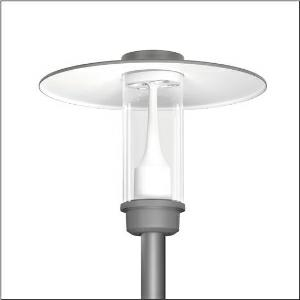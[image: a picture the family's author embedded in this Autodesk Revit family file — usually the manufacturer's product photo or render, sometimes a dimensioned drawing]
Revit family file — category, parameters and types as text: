
# Revit family: litepole_2_iq___p1_0a_5xa5425ff14h_a7e5
name_source: partatom
category: Lighting Fixtures
units: mm (PartAtom-declared; Revit-internal decimal feet)

## family parameters
Cut with Voids When Loaded = No
Host = Face
Light Source = No
Part Type = Normal
Room Calculation Point = No
Round Connector Dimension = Use Diameter
Shared = No

## types (1)
- --- (1 x LED, 1520 lm, 10.5 W, 3000K)
    Apparent Load = 11 VA
    CIE Flux Codes = 33 62 89 96 100
    Color Rendering = 70
    Color Temperature = 3000K
    Default Elevation = 1800 mm
    Description = Litepole 2 iQ, mast luminaire, Module 540 iQ-SR, primary light control with 3 zone facetted reflector, of plastic, silver coated, highly specular, structured, primary optical cover: cover, of PMMA, transparent, light distribution: P1.0a, light emission: direct distribution, primary light characteristic: strongly asymmetric, installation type: post-top, LED, High Power LED, rated luminous flux: 1.520lm, luminous efficacy: 145lm/W, light colour: 730, colour temperature: 3000K, control gear: iQ Street-Remote, control: Auto-Match, Temp-Guard, Lumen-Switch, Night-Set, Smart-Wire, Light-Fading, Desk-Remote (wireless, voltage-free reading and setting of iQ features in the workshop via application-optimized NFC function/RFID function), optimised constant luminous flux control (CLO 2.0), Street-Remote, pre-setting: logarithmic dimming characteristic, with terminal, 6-pole, max. 2.5mm², mains connection: 230..240V, AC, 50/60Hz, start of lifetime: 11W, end of service life: 11W, reduction: 5W, luminaire housing, upper part, of aluminium, coated, Siteco® metallic grey (DB 702S), diameter: 750mm, height: 590mm, spigot size: d x l = 76 x 70mm (post-top) | with reducer (optional accessory) 60 x 70mm, mounting height: 3..5m, post-top mast mounting element, of diecast aluminium, coated, Siteco® metallic grey (DB 702S), Module 540 iQ-SR, traffic white (RAL 9016), equipment: standard, protection rating (complete): IP65, insulation class (complete): insulation class II (safety insulation), certification: CE, ENEC, VDE, packaging unit: 1 piece

Light Distribution: P1.0a
    Height = 590 mm
    Lamp = 1 x LED
    Lamp Light Flux = 1520 lm
    Lamp Power = 10.5 W
    Lamp count = 1
    Length = 750 mm
    Luminous efficacy = 145 lm/W
    Manufacturer = Siteco
    ModVariant = No
    Model = 5XA5425FF14H
    Number of Poles = 1
    OnlyDefault = Yes
    Power Factor = 1
    Product Name = Litepole 2 iQ | P1.0a
    Product group = mast luminaire | pylon top
    ProductGroupID = 6100
    Protection Class = Protection class II
    Protection Degree = IP 65
    RLX_Detail_Level = 1
    RLX_Emergency_Light_Flux = 0 lm
    RLX_Emergency_Type = 0
    RLX_Emergency_Type_DB = No
    RlxData = <blob elided: 55361 chars, md5=980627de>
    Socket = socket
    Standby Power = 0 W
    System Light Flux = 1520 lm
    System Power = 11 W
    Type Comments = factory setting: luminous flux: 100 % | dim-lin: 254 | 419 mA
    Type Image = l_1006518.jpg
    URL = http://relux.com
    VarID = @adj_189977
    Voltage = 0 V
    Weight = 0.00 kg
    Width = 0 mm  [stored 0 ft]

note: [stored X ft] marks values corroborated as IEEE doubles in the binary element streams (Revit-internal decimal feet)

## geometry (parser evidence)
native form markers: Blend x4, Sweep x11
no freeform markers — native parametric forms only
